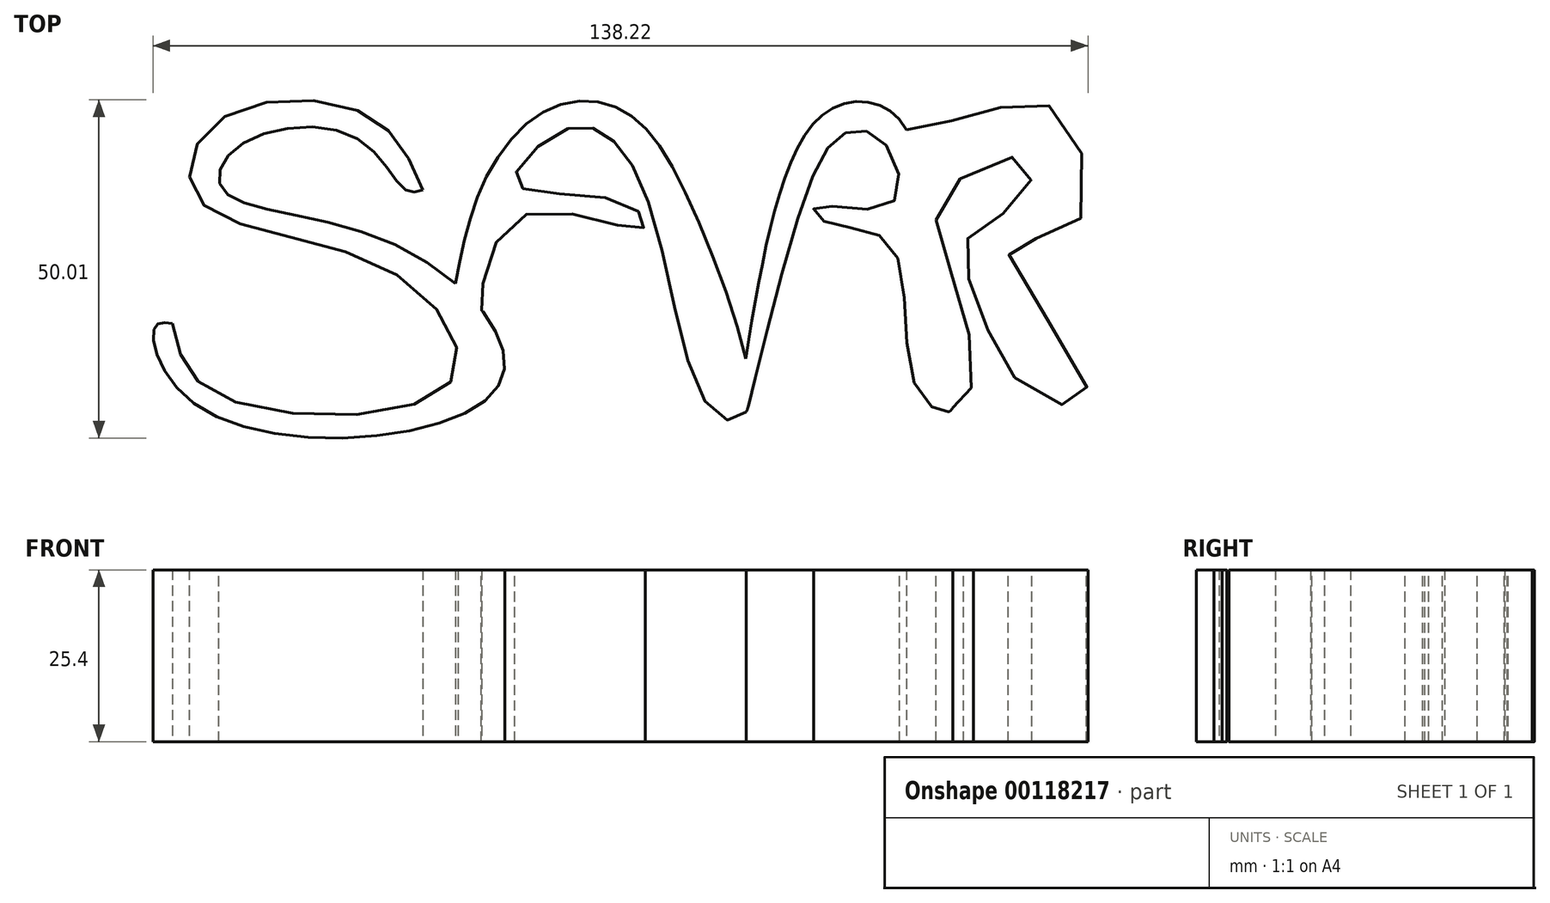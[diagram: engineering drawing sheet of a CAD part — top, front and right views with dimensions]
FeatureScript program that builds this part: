
annotation { "Feature Type Name" : "Feature", "Feature Type Description" : "" }
export const myFeature = defineFeature(function(context is Context, id is Id, definition is map)
    precondition{}
    {
        {
            var Q0;
            Q0=qCreatedBy(makeId("Top.planeOp"),FACE);
            var sketch = newSketch(context, id + "F0", { "sketchPlane" : qUnion([Q0])});
            skFitSpline(sketch, "E0", {"points": [v(-24.68, 32.8) * mm, v(-33.1, 43.97) * mm, v(-55.23, 42.8) * mm, v(-57.78, 31.24) * mm, v(-29.58, 20.86) * mm, v(-20.76, 4.21) * mm, v(-54.84, 2.45) * mm, v(-61.7, 13.02) * mm], "startDerivative": vector(-45.6, 109.04) * mm, "endDerivative": vector(-21.51, 105.78) * mm});
            skFitSpline(sketch, "E1", {"points": [v(-24.68, 32.8) * mm, v(-27.22, 32.8) * mm, v(-34.47, 40.45) * mm, v(-51.9, 39.27) * mm, v(-54.25, 32.8) * mm, v(-28.99, 24.78) * mm, v(-13.51, 3.82) * mm, v(-56.6, 0) * mm, v(-64.24, 12.63) * mm, v(-61.7, 13.02) * mm], "startDerivative": vector(-54.12, -17) * mm, "endDerivative": vector(65.23, -10.93) * mm});
            skFitSpline(sketch, "E2", {"points": [v(-19.83, 18.93) * mm, v(-15.47, 34.37) * mm, v(-5.68, 44.95) * mm, v(4.9, 44.56) * mm, v(15.28, 29.87) * mm, v(23.11, 0) * mm, v(18.22, 0) * mm, v(9.6, 28.1) * mm, v(2.55, 40.84) * mm, v(-4.3, 41.43) * mm, v(-10.97, 33.79) * mm, v(5.29, 30.85) * mm, v(7.83, 27.13) * mm, v(-10.58, 28.7) * mm, v(-16.02, 15.05) * mm, v(-15.83, 14.81) * mm], "startDerivative": vector(39.58, 210.25) * mm, "endDerivative": vector(20.8, -6.12) * mm});
            skFitSpline(sketch, "E3", {"points": [v(23.05, 7.84) * mm, v(28, 32.02) * mm, v(35.65, 44.75) * mm, v(44.85, 44.17) * mm, v(50.14, 28.1) * mm, v(53.67, 5.58) * mm, v(53.08, 0) * mm, v(47.99, 4.21) * mm, v(44.46, 24.78) * mm, v(34.67, 28.1) * mm, v(33.3, 30.26) * mm, v(44.46, 30.65) * mm, v(43.48, 39.86) * mm, v(37.8, 41.23) * mm, v(31.34, 30.46) * mm, v(23.42, 0.8) * mm, v(23.11, 0) * mm], "startDerivative": vector(45.12, 274.65) * mm, "endDerivative": vector(-18.6, -22.38) * mm});
            skFitSpline(sketch, "E4", {"points": [v(46.8, 41.7) * mm, v(57.98, 44.17) * mm, v(69.53, 44.17) * mm, v(71.3, 26.93) * mm, v(61.9, 24.38) * mm, v(73.64, 2.45) * mm, v(65.42, 2.84) * mm, v(57.58, 15.38) * mm, v(55.82, 25.56) * mm, v(63.85, 31.44) * mm, v(64.24, 37.31) * mm, v(52.3, 32.02) * mm, v(53.67, 19.88) * mm, v(56.21, 3.04) * mm, v(53.67, 0.63) * mm, v(53.08, 0) * mm], "startDerivative": vector(154.73, 27.58) * mm, "endDerivative": vector(-21.98, -32.28) * mm});
            skSolve(sketch);
        }
        {
            var Q0;
            Q0 = qSketchRegion(id + "F0", true);
            extrude(context, id + "F1", {"entities" : qUnion([Q0]), "depth" : 25.4 * mm});
        }
    });
